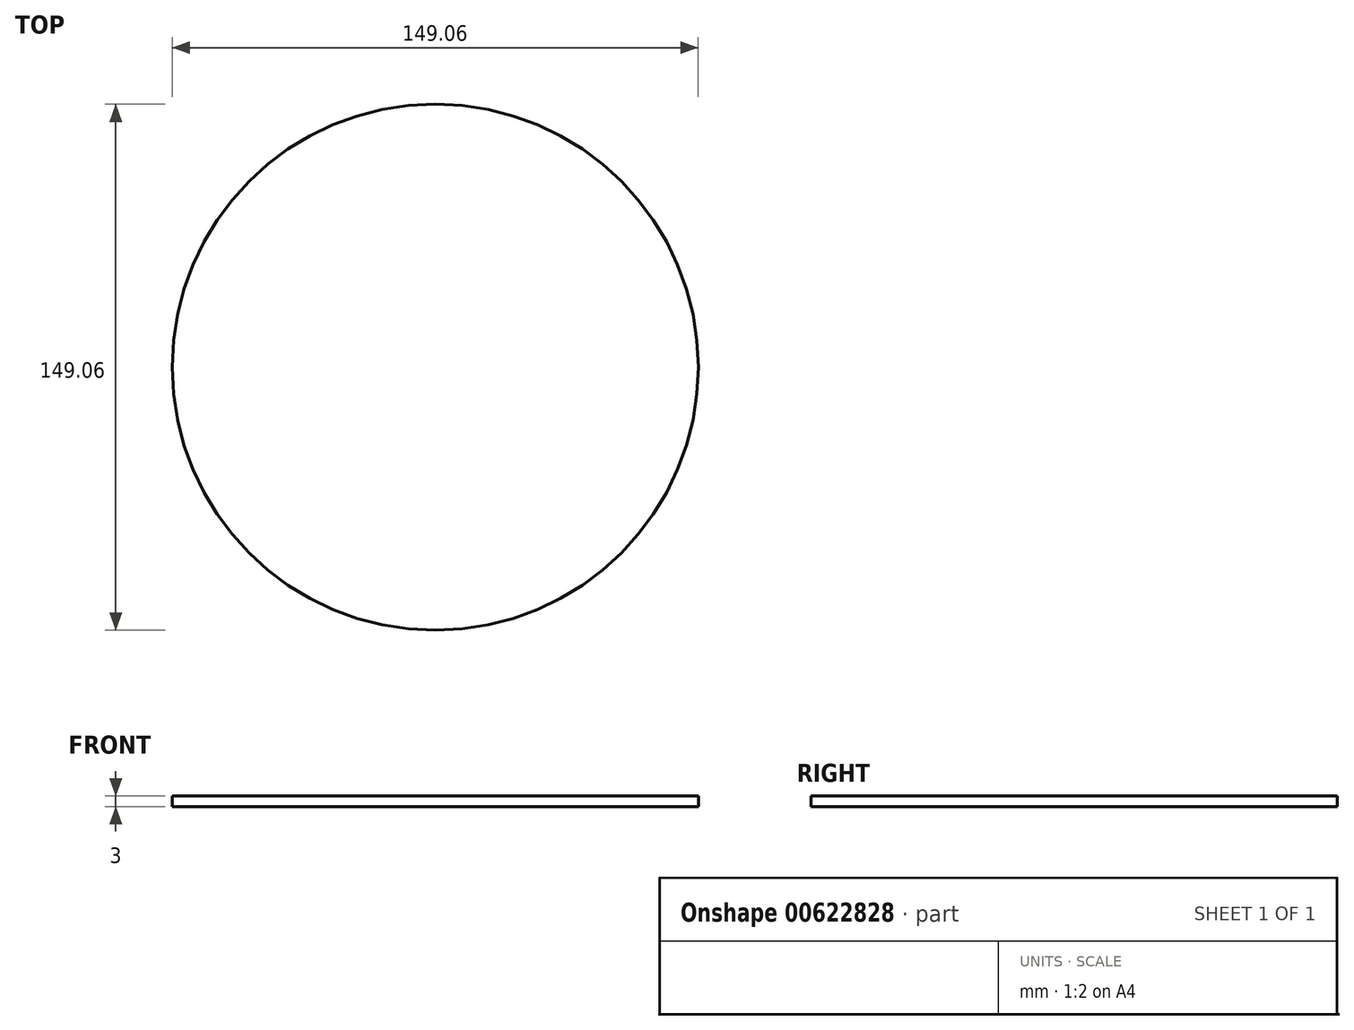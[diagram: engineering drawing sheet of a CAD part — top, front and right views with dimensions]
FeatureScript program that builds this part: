
annotation { "Feature Type Name" : "Feature", "Feature Type Description" : "" }
export const myFeature = defineFeature(function(context is Context, id is Id, definition is map)
    precondition{}
    {
        {
            var Q0;
            Q0=qCreatedBy(makeId("Top.planeOp"),FACE);
            var sketch = newSketch(context, id + "F0", { "sketchPlane" : qUnion([Q0])});
            skCircle(sketch, "E0", {"center": v(0, 0) * mm, "radius": 74.53 * mm});
            skSolve(sketch);
        }
        {
            var Q0;
            Q0 = qSketchRegion(id + "F0", true);
            extrude(context, id + "F1", {"entities" : qUnion([Q0]), "depth" : 3 * mm, "offsetDistance" : 25 * mm});
        }
    });
